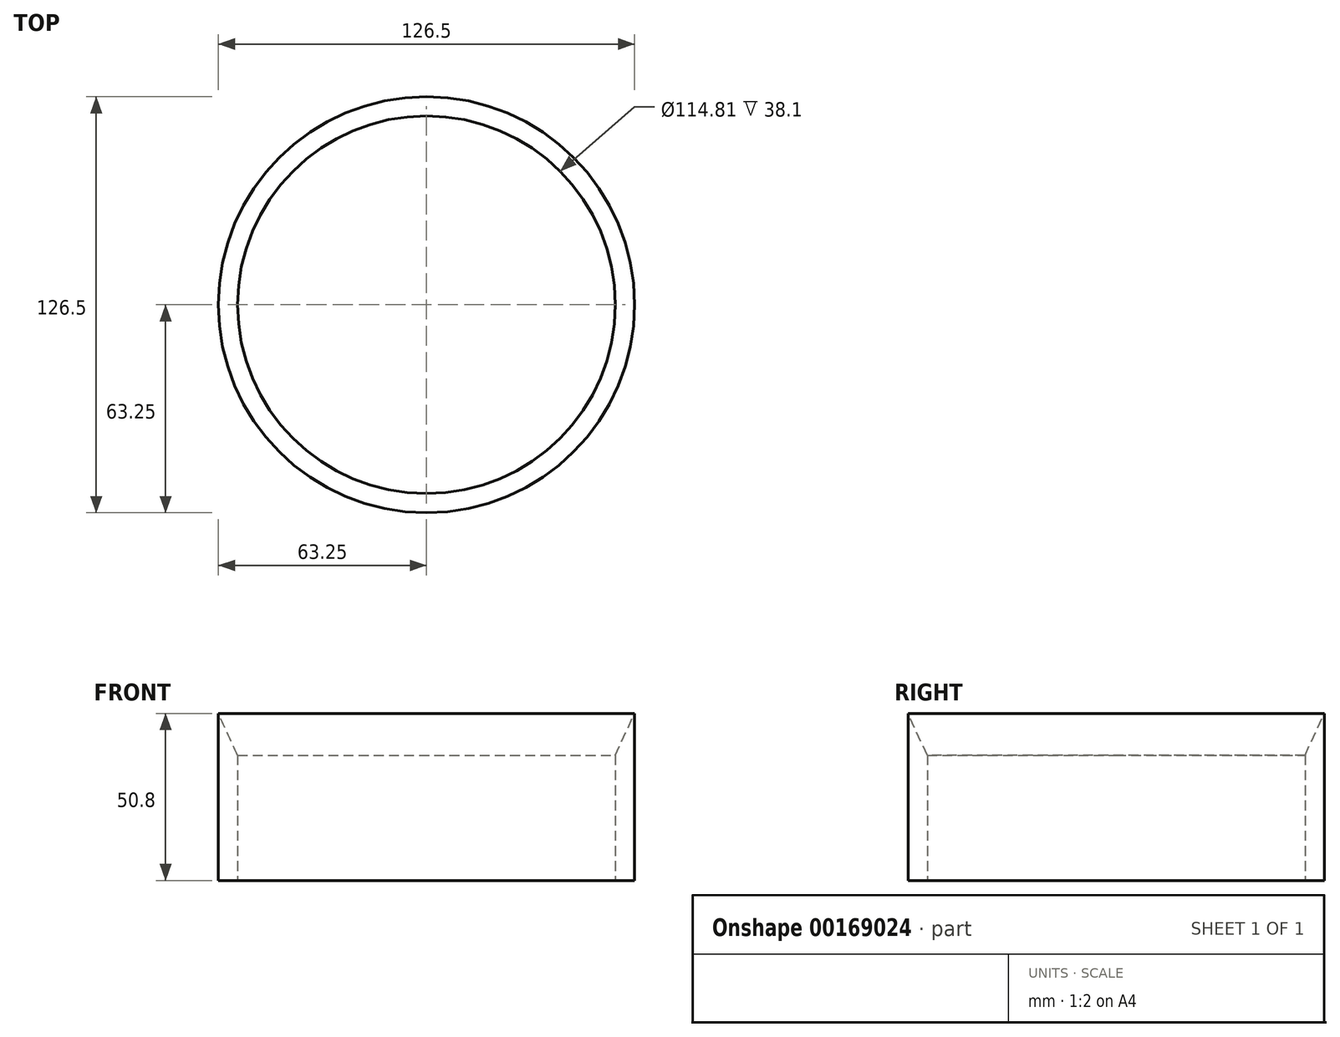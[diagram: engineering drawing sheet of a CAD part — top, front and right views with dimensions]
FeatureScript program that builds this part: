
annotation { "Feature Type Name" : "Feature", "Feature Type Description" : "" }
export const myFeature = defineFeature(function(context is Context, id is Id, definition is map)
    precondition{}
    {
        {
            var Q0;
            Q0=qCreatedBy(makeId("Front.planeOp"),FACE);
            var sketch = newSketch(context, id + "F0", { "sketchPlane" : qUnion([Q0])});
            skLineSegment(sketch, "E0", {"start": v(0, 0) * mm, "end": v(0, 54.13) * mm, "construction": true});
            skLineSegment(sketch, "E1", {"start": v(-63.25, 0) * mm, "end": v(-63.25, 50.8) * mm});
            skLineSegment(sketch, "E2", {"start": v(-63.25, 50.8) * mm, "end": v(-57.4, 38.1) * mm});
            skLineSegment(sketch, "E3", {"start": v(-57.4, 38.1) * mm, "end": v(-57.4, 0) * mm});
            skLineSegment(sketch, "E4", {"start": v(-57.4, 0) * mm, "end": v(-63.25, 0) * mm});
            skSolve(sketch);
        }
        {
            var Q0;
            Q0=makeQuery(id+"F0.imprint","IMPRINT",FACE,{"disambiguationData":[TD([[makeQuery(id+"F0.imprint","IMPRINT",EDGE,{"derivedFrom":sQuery(id+"F0.wireOp",EDGE,"E1")}),-1.0]])]});
            var Q1;
            Q1=sQuery(id+"F0.wireOp",EDGE,"E0");
            revolve(context, id + "F1", {"entities" : qUnion([Q0]), "axis" : qUnion([Q1]), "revolveType" : RevolveType.FULL});
        }
    });
